# Revit family: 601-A-009-DN225-300
name_source: partatom
category: Pipe Accessories
units: mm (PartAtom-declared; Revit-internal decimal feet)

## family parameters
Always vertical = Yes
Cut with Voids When Loaded = No
Part Type = Valve - Breaks Into
Round Connector Dimension = Use Diameter
Shared = No
Work Plane-Based = No

## types (6) — shared parameters
DN225_242-268 = 601-268-000-6100
DN250_266-292 = 601-292-000-6100
DN250_280-306 = 601-306-000-6100
DN300_301-327 = 601-327-000-6100
DN300_324-350 = 601-350-000-6100
DN300_352-378 = 601-378-000-6100
Description_ = AVK UNIVERSAL SUPA® STRAIGHT COUPLING
F = 5 mm  [stored 0.0164042 ft]
Search_Table = 601-A-009-DN225-300
URL_product_pages = https://www.avkvalves.com
W1 = 32 mm  [stored 0.104987 ft]

## per-type parameters (varying)
| type | B2 | Body_height | Body_height_ref | D1 | D2 | D3 | DN | DN2 | DN_ref | ID | L | L1 | PCD | PCD_Ref | W2 |
| DN225_242-268 | 106 mm | 211 mm  [stored 0.692257 ft] | 199 mm  [stored 0.652887 ft] | 165 mm | 150 mm | 386 mm | 225 mm  [stored 0.738189 ft] | 268 mm  [stored 0.879265 ft] | 134 mm | 113 mm | 237 mm | 140 mm  [stored 0.459318 ft] | 350 mm | 374 mm | 188 mm  [stored 0.616798 ft] |
| DN250_266-292 | 116 mm | 231 mm  [stored 0.757874 ft] | 219 mm  [stored 0.718504 ft] | 178 mm  [stored 0.58399 ft] | 160 mm  [stored 0.524934 ft] | 411 mm | 250 mm  [stored 0.82021 ft] | 292 mm  [stored 0.958005 ft] | 146 mm  [stored 0.479003 ft] | 125 mm  [stored 0.410105 ft] | 257 mm | 160 mm  [stored 0.524934 ft] | 374 mm | 398 mm | 201 mm |
| DN250_280-306 | 116 mm | 231 mm  [stored 0.757874 ft] | 219 mm  [stored 0.718504 ft] | 184 mm  [stored 0.603675 ft] | 164 mm  [stored 0.538058 ft] | 425 mm | 250 mm  [stored 0.82021 ft] | 306 mm  [stored 1.00394 ft] | 153 mm  [stored 0.501969 ft] | 125 mm  [stored 0.410105 ft] | 257 mm | 160 mm  [stored 0.524934 ft] | 388 mm | 412 mm | 208 mm |
| DN300_301-327 | 116 mm | 231 mm  [stored 0.757874 ft] | 219 mm  [stored 0.718504 ft] | 194 mm  [stored 0.636483 ft] | 175 mm  [stored 0.574147 ft] | 445 mm | 300 mm  [stored 0.984252 ft] | 327 mm | 164 mm  [stored 0.538058 ft] | 150 mm | 257 mm | 160 mm  [stored 0.524934 ft] | 405 mm | 429 mm | 218 mm  [stored 0.715223 ft] |
| DN300_324-350 | 116 mm | 231 mm  [stored 0.757874 ft] | 219 mm  [stored 0.718504 ft] | 205 mm  [stored 0.672572 ft] | 187 mm  [stored 0.613517 ft] | 469 mm | 300 mm  [stored 0.984252 ft] | 350 mm | 175 mm  [stored 0.574147 ft] | 150 mm | 257 mm | 160 mm  [stored 0.524934 ft] | 428 mm | 452 mm | 230 mm |
| DN300_352-378 | 116 mm | 231 mm  [stored 0.757874 ft] | 219 mm  [stored 0.718504 ft] | 205 mm  [stored 0.672572 ft] | 195 mm  [stored 0.639764 ft] | 469 mm | 300 mm  [stored 0.984252 ft] | 378 mm | 189 mm  [stored 0.620079 ft] | 150 mm | 277 mm | 160 mm  [stored 0.524934 ft] | 428 mm | 452 mm | 230 mm |

note: [stored X ft] marks values corroborated as IEEE doubles in the binary element streams (Revit-internal decimal feet)

## geometry (parser evidence)
native form markers: Sweep x4
no freeform markers — native parametric forms only
